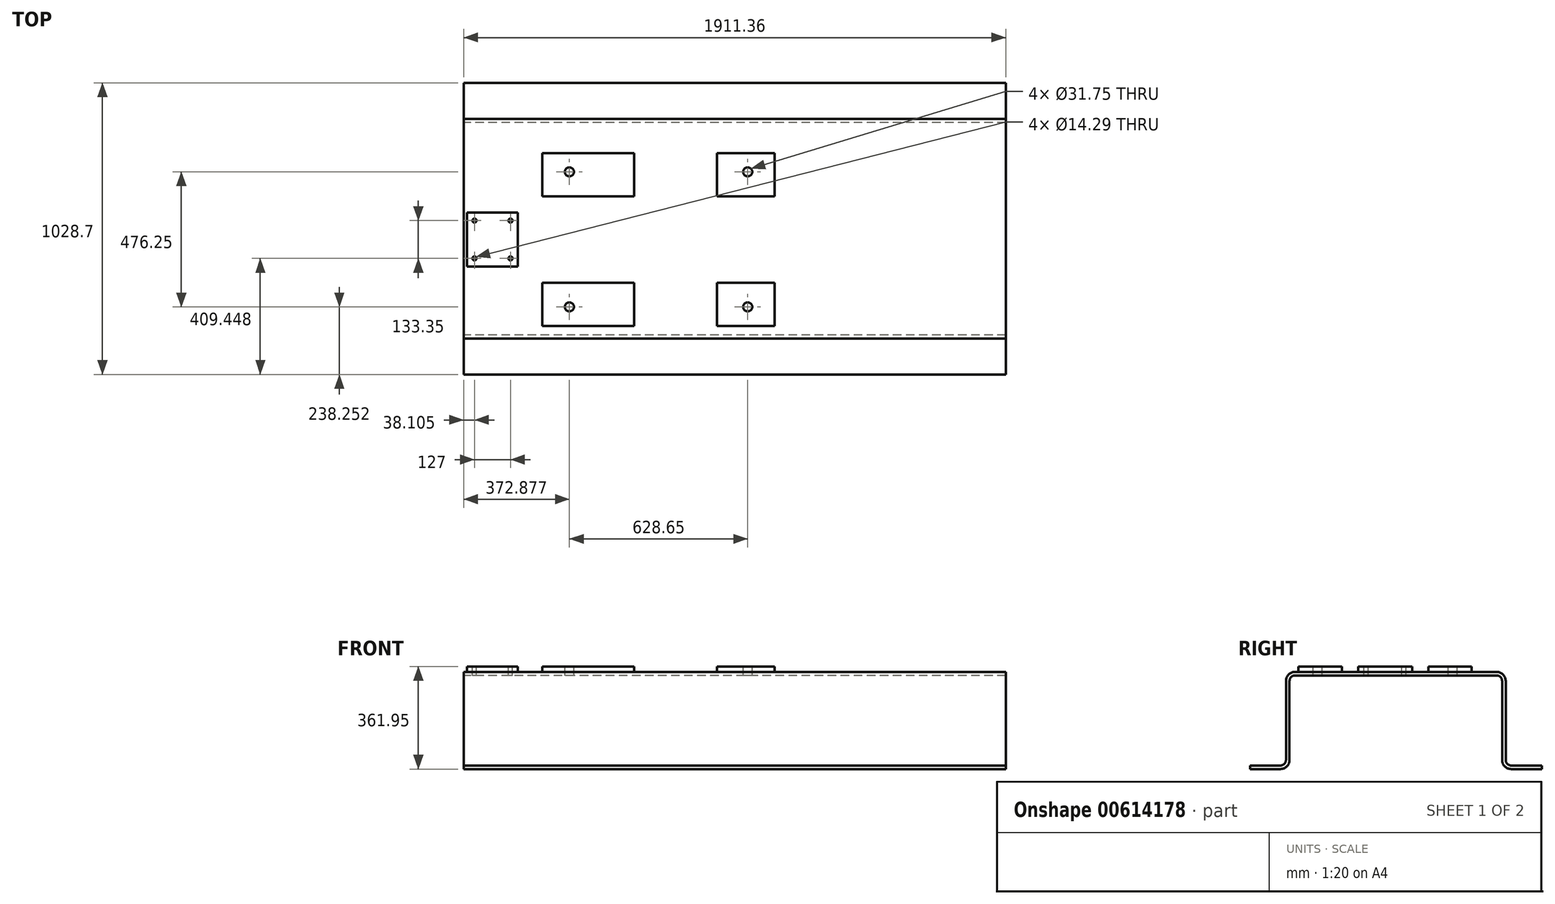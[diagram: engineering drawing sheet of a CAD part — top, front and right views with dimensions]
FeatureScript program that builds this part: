
annotation { "Feature Type Name" : "Feature", "Feature Type Description" : "" }
export const myFeature = defineFeature(function(context is Context, id is Id, definition is map)
    precondition{}
    {
        {
            var Q0;
            Q0=qCreatedBy(makeId("Right.planeOp"),FACE);
            var sketch = newSketch(context, id + "F0", { "sketchPlane" : qUnion([Q0])});
            skLineSegment(sketch, "E0.bottom", {"start": v(-355.6, 171.45) * mm, "end": v(0, 171.45) * mm});
            skLineSegment(sketch, "E0.top", {"start": v(-514.35, -171.45) * mm, "end": v(-406.4, -171.45) * mm});
            skLineSegment(sketch, "E0.left", {"start": v(-514.35, -158.75) * mm, "end": v(-514.35, -171.45) * mm});
            skLineSegment(sketch, "E0.right", {"start": v(514.35, 171.45) * mm, "end": v(514.35, -171.45) * mm});
            skPoint(sketch, "E0.middle", {"position": v(0, 0) * mm});
            skLineSegment(sketch, "E1.0", {"start": v(-387.35, 139.7) * mm, "end": v(-387.35, -139.7) * mm});
            skLineSegment(sketch, "E2", {"start": v(0, 292.84) * mm, "end": v(0, -241.27) * mm, "construction": true});
            skLineSegment(sketch, "E3.0", {"start": v(-355.6, 158.75) * mm, "end": v(0, 158.75) * mm});
            skLineSegment(sketch, "E4.0", {"start": v(-374.65, 139.7) * mm, "end": v(-374.65, -139.7) * mm});
            skLineSegment(sketch, "E5.0", {"start": v(-514.35, -158.75) * mm, "end": v(-406.4, -158.75) * mm});
            skArc(sketch, "E6.filletArc", {"start": v(-406.4, -158.75) * mm, "mid": v(-392.93, -153.17) * mm, "end": v(-387.35, -139.7) * mm});
            skArc(sketch, "E7.filletArc", {"start": v(-355.6, 158.75) * mm, "mid": v(-369.07, 153.17) * mm, "end": v(-374.65, 139.7) * mm});
            skPoint(sketch, "E8.newPointA", {"position": v(514.35, -171.45) * mm});
            skArc(sketch, "E8.filletArc", {"start": v(-406.4, -171.45) * mm, "mid": v(-383.95, -162.15) * mm, "end": v(-374.65, -139.7) * mm});
            skPoint(sketch, "E9.newPointB", {"position": v(-514.35, 171.45) * mm});
            skArc(sketch, "E9.filletArc", {"start": v(-355.6, 171.45) * mm, "mid": v(-378.05, 162.15) * mm, "end": v(-387.35, 139.7) * mm});
            skLineSegment(sketch, "E10", {"start": v(0, 171.45) * mm, "end": v(0, 158.75) * mm});
            skSolve(sketch);
        }
        {
            var Q0;
            Q0 = qSketchRegion(id + "F0", true);
            extrude(context, id + "F1", {"entities" : qUnion([Q0]), "endBound" : BoundingType.SYMMETRIC, "depth" : 1911.35 * mm, "offsetDistance" : 25.4 * mm});
        }
        {
            var Q0;
            Q0=makeQuery(id+"F1.opExtrude","SWEPT_BODY",BODY,{"disambiguationData":[OSD([sQuery(id+"F0.wireOp",EDGE,"E0.bottom"),sQuery(id+"F0.wireOp",EDGE,"E0.top"),sQuery(id+"F0.wireOp",EDGE,"E0.left"),sQuery(id+"F0.wireOp",EDGE,"E1.0"),sQuery(id+"F0.wireOp",EDGE,"E3.0"),sQuery(id+"F0.wireOp",EDGE,"E4.0"),sQuery(id+"F0.wireOp",EDGE,"E5.0"),sQuery(id+"F0.wireOp",EDGE,"E6.filletArc"),sQuery(id+"F0.wireOp",EDGE,"E7.filletArc"),sQuery(id+"F0.wireOp",EDGE,"E8.filletArc"),sQuery(id+"F0.wireOp",EDGE,"E9.filletArc"),sQuery(id+"F0.wireOp",EDGE,"E10")])]});
            var Q1;
            Q1=qCreatedBy(makeId("Front.planeOp"),FACE);
            mirror(context, id + "F2", {"operationType" : NewBodyOperationType.ADD, "entities" : qUnion([Q0]), "mirrorPlane" : qUnion([Q1])});
        }
        {
            var Q0;
            {var subQ0=makeQuery(id+"F1.opExtrude","SWEPT_FACE",FACE,{"disambiguationData":[OSD([sQuery(id+"F0.wireOp",EDGE,"E0.bottom")])]});Q0=makeQuery(id+"F2.boolean.opBoolean","MERGE",FACE,{"derivedFrom":[subQ0,makeQuery(id+"F2.opPattern","COPY",FACE,{"derivedFrom":subQ0,"instanceName":"1"})]});}
            var sketch = newSketch(context, id + "F3", { "sketchPlane" : qUnion([Q0])});
            skLineSegment(sketch, "E11.0", {"start": v(955.68, 165.1) * mm, "end": v(417.16, 165.1) * mm, "construction": true});
            skLineSegment(sketch, "E12.0", {"start": v(293.14, -38.1) * mm, "end": v(-955.68, -38.1) * mm, "construction": true});
            skLineSegment(sketch, "E13.0", {"start": v(141.1, -190.5) * mm, "end": v(-62.1, -190.5) * mm});
            skLineSegment(sketch, "E14.0", {"start": v(141.1, -342.9) * mm, "end": v(-62.1, -342.9) * mm});
            skLineSegment(sketch, "E15.0", {"start": v(141.1, 114.3) * mm, "end": v(-62.1, 114.3) * mm});
            skLineSegment(sketch, "E16.0", {"start": v(141.1, 266.7) * mm, "end": v(-62.1, 266.7) * mm});
            skLineSegment(sketch, "E17.0", {"start": v(644.52, -779.36) * mm, "end": v(644.52, 355.6) * mm, "construction": true});
            skLineSegment(sketch, "E18.0", {"start": v(-268.35, -779.36) * mm, "end": v(-268.35, 355.6) * mm, "construction": true});
            skLineSegment(sketch, "E19.0", {"start": v(-62.1, -342.9) * mm, "end": v(-62.1, -190.5) * mm});
            skLineSegment(sketch, "E20.0", {"start": v(141.1, -342.9) * mm, "end": v(141.1, -190.5) * mm});
            skLineSegment(sketch, "E21.0", {"start": v(-354.2, -342.9) * mm, "end": v(-354.2, -190.5) * mm});
            skLineSegment(sketch, "E22.0", {"start": v(-678.05, -342.9) * mm, "end": v(-678.05, -190.5) * mm});
            skLineSegment(sketch, "E23.trimOffspring", {"start": v(-354.2, 266.7) * mm, "end": v(-678.05, 266.7) * mm});
            skLineSegment(sketch, "E24.trimOffspring", {"start": v(-354.2, 114.3) * mm, "end": v(-678.05, 114.3) * mm});
            skLineSegment(sketch, "E25.trimOffspring", {"start": v(-354.2, -190.5) * mm, "end": v(-678.05, -190.5) * mm});
            skLineSegment(sketch, "E26.trimOffspring", {"start": v(-354.2, -342.9) * mm, "end": v(-678.05, -342.9) * mm});
            skLineSegment(sketch, "E27.trimOffspring", {"start": v(141.1, 114.3) * mm, "end": v(141.1, 266.7) * mm});
            skLineSegment(sketch, "E28.trimOffspring", {"start": v(-62.1, 114.3) * mm, "end": v(-62.1, 266.7) * mm});
            skLineSegment(sketch, "E29.trimOffspring", {"start": v(-678.05, 114.3) * mm, "end": v(-678.05, 266.7) * mm});
            skLineSegment(sketch, "E30.trimOffspring", {"start": v(-354.2, 114.3) * mm, "end": v(-354.2, 266.7) * mm});
            skSolve(sketch);
        }
        {
            var Q0;
            Q0 = qSketchRegion(id + "F3", true);
            extrude(context, id + "F4", {"entities" : qUnion([Q0]), "operationType" : NewBodyOperationType.ADD, "depth" : 19.05 * mm, "offsetDistance" : 25.4 * mm});
        }
        {
            var Q0;
            Q0=makeQuery(id+"F4.opExtrude","CAP_FACE",FACE,{"disambiguationData":[OSD([sQuery(id+"F3.wireOp",EDGE,"E23.trimOffspring"),sQuery(id+"F3.wireOp",EDGE,"E24.trimOffspring"),sQuery(id+"F3.wireOp",EDGE,"E29.trimOffspring"),sQuery(id+"F3.wireOp",EDGE,"E30.trimOffspring")])],"isStart":false});
            var sketch = newSketch(context, id + "F5", { "sketchPlane" : qUnion([Q0])});
            skLineSegment(sketch, "E31.0", {"start": v(-268.35, -779.36) * mm, "end": v(-268.35, 355.6) * mm, "construction": true});
            skLineSegment(sketch, "E32.0", {"start": v(293.14, -38.1) * mm, "end": v(-955.68, -38.1) * mm, "construction": true});
            skLineSegment(sketch, "E33.0", {"start": v(293.14, 200.15) * mm, "end": v(-955.68, 200.15) * mm, "construction": true});
            skLineSegment(sketch, "E34.0", {"start": v(293.14, -276.1) * mm, "end": v(-955.68, -276.1) * mm, "construction": true});
            skLineSegment(sketch, "E35.0", {"start": v(-582.8, -779.36) * mm, "end": v(-582.8, 355.6) * mm, "construction": true});
            skLineSegment(sketch, "E36.0", {"start": v(45.85, -779.36) * mm, "end": v(45.85, 355.6) * mm, "construction": true});
            skPoint(sketch, "E37", {"position": v(-582.8, 200.15) * mm});
            skPoint(sketch, "E38", {"position": v(45.85, 200.15) * mm});
            skPoint(sketch, "E39", {"position": v(45.85, -276.1) * mm});
            skPoint(sketch, "E40", {"position": v(-582.8, -276.1) * mm});
            skSolve(sketch);
        }
        {
            var Q0;
            Q0=sQuery(id+"F5.wireOp",VERTEX,"E37");
            var Q1;
            Q1=sQuery(id+"F5.wireOp",VERTEX,"E40");
            var Q2;
            Q2=sQuery(id+"F5.wireOp",VERTEX,"E38");
            var Q3;
            Q3=sQuery(id+"F5.wireOp",VERTEX,"E39");
            var Q4;
            Q4=makeQuery(id+"F1.opExtrude","SWEPT_BODY",BODY,{"disambiguationData":[OSD([sQuery(id+"F0.wireOp",EDGE,"E0.bottom"),sQuery(id+"F0.wireOp",EDGE,"E0.top"),sQuery(id+"F0.wireOp",EDGE,"E0.left"),sQuery(id+"F0.wireOp",EDGE,"E1.0"),sQuery(id+"F0.wireOp",EDGE,"E3.0"),sQuery(id+"F0.wireOp",EDGE,"E4.0"),sQuery(id+"F0.wireOp",EDGE,"E5.0"),sQuery(id+"F0.wireOp",EDGE,"E6.filletArc"),sQuery(id+"F0.wireOp",EDGE,"E7.filletArc"),sQuery(id+"F0.wireOp",EDGE,"E8.filletArc"),sQuery(id+"F0.wireOp",EDGE,"E9.filletArc"),sQuery(id+"F0.wireOp",EDGE,"E10")])]});
            hole(context, id + "F6", {"style" : HoleStyle.SIMPLE, "endStyle" : HoleEndStyle.THROUGH, "holeDiameter" : 31.75 * mm, "majorDiameter" : 9.52 * mm, "isTappedThrough" : true, "tappedDepth" : 25.4 * mm, "tapClearance" : 3, "locations" : qUnion([Q0, Q1, Q2, Q3]), "scope" : qUnion([Q4])});
        }
        {
            var Q0;
            Q0=makeQuery(id+"F3.imprint","IMPRINT",FACE,{"disambiguationData":[TD([[makeQuery(id+"F3.imprint","IMPRINT",EDGE,{"derivedFrom":sQuery(id+"F3.wireOp",EDGE,"E13.0")}),-1.0]])]});
            var sketch = newSketch(context, id + "F7", { "sketchPlane" : qUnion([Q0])});
            skLineSegment(sketch, "E41.0", {"start": v(293.14, -38.1) * mm, "end": v(-955.68, -38.1) * mm, "construction": true});
            skLineSegment(sketch, "E42.0", {"start": v(-678.05, -38.1) * mm, "end": v(-678.05, 266.7) * mm, "construction": true});
            skPoint(sketch, "E43.orphan", {"position": v(-678.05, 114.3) * mm});
            skLineSegment(sketch, "E44.0", {"start": v(-765.43, -38.1) * mm, "end": v(-765.43, 57.15) * mm});
            skLineSegment(sketch, "E45.0", {"start": v(-943.23, -38.1) * mm, "end": v(-943.23, 57.15) * mm});
            skLineSegment(sketch, "E46.0", {"start": v(-765.43, 57.15) * mm, "end": v(-943.23, 57.15) * mm});
            skLineSegment(sketch, "E47.MirrorCS", {"start": v(-765.43, -38.1) * mm, "end": v(-765.43, -133.35) * mm});
            skLineSegment(sketch, "E48.MirrorCS", {"start": v(-765.43, -133.35) * mm, "end": v(-943.23, -133.35) * mm});
            skLineSegment(sketch, "E49.MirrorCS", {"start": v(-943.23, -38.1) * mm, "end": v(-943.23, -133.35) * mm});
            skSolve(sketch);
        }
        {
            var Q0;
            Q0 = qSketchRegion(id + "F7", true);
            extrude(context, id + "F8", {"entities" : qUnion([Q0]), "operationType" : NewBodyOperationType.ADD, "depth" : 19.05 * mm, "offsetDistance" : 25.4 * mm});
        }
        {
            var Q0;
            Q0=makeQuery(id+"F8.opExtrude","CAP_FACE",FACE,{"disambiguationData":[OSD([sQuery(id+"F7.wireOp",EDGE,"E44.0"),sQuery(id+"F7.wireOp",EDGE,"E45.0"),sQuery(id+"F7.wireOp",EDGE,"E46.0"),sQuery(id+"F7.wireOp",EDGE,"E47.MirrorCS"),sQuery(id+"F7.wireOp",EDGE,"E48.MirrorCS"),sQuery(id+"F7.wireOp",EDGE,"E49.MirrorCS")])],"isStart":false});
            var sketch = newSketch(context, id + "F9", { "sketchPlane" : qUnion([Q0])});
            skLineSegment(sketch, "E50.0", {"start": v(293.14, -38.1) * mm, "end": v(-955.68, -38.1) * mm, "construction": true});
            skLineSegment(sketch, "E51.0", {"start": v(-268.35, -779.36) * mm, "end": v(-268.35, 355.6) * mm, "construction": true});
            skLineSegment(sketch, "E52.0", {"start": v(-790.58, -779.36) * mm, "end": v(-790.58, 355.6) * mm, "construction": true});
            skLineSegment(sketch, "E53.0", {"start": v(-917.58, -779.36) * mm, "end": v(-917.58, 355.6) * mm, "construction": true});
            skLineSegment(sketch, "E54.0", {"start": v(293.14, 28.45) * mm, "end": v(-955.68, 28.45) * mm, "construction": true});
            skLineSegment(sketch, "E55.0", {"start": v(293.14, -104.9) * mm, "end": v(-955.68, -104.9) * mm, "construction": true});
            skPoint(sketch, "E56", {"position": v(-917.58, 28.45) * mm});
            skPoint(sketch, "E57", {"position": v(-790.58, 28.45) * mm});
            skPoint(sketch, "E58", {"position": v(-790.58, -104.9) * mm});
            skPoint(sketch, "E59", {"position": v(-917.58, -104.9) * mm});
            skSolve(sketch);
        }
        {
            var Q0;
            Q0=sQuery(id+"F9.wireOp",VERTEX,"E56");
            var Q1;
            Q1=sQuery(id+"F9.wireOp",VERTEX,"E57");
            var Q2;
            Q2=sQuery(id+"F9.wireOp",VERTEX,"E59");
            var Q3;
            Q3=sQuery(id+"F9.wireOp",VERTEX,"E58");
            var Q4;
            Q4=makeQuery(id+"F1.opExtrude","SWEPT_BODY",BODY,{"disambiguationData":[OSD([sQuery(id+"F0.wireOp",EDGE,"E0.bottom"),sQuery(id+"F0.wireOp",EDGE,"E0.top"),sQuery(id+"F0.wireOp",EDGE,"E0.left"),sQuery(id+"F0.wireOp",EDGE,"E1.0"),sQuery(id+"F0.wireOp",EDGE,"E3.0"),sQuery(id+"F0.wireOp",EDGE,"E4.0"),sQuery(id+"F0.wireOp",EDGE,"E5.0"),sQuery(id+"F0.wireOp",EDGE,"E6.filletArc"),sQuery(id+"F0.wireOp",EDGE,"E7.filletArc"),sQuery(id+"F0.wireOp",EDGE,"E8.filletArc"),sQuery(id+"F0.wireOp",EDGE,"E9.filletArc"),sQuery(id+"F0.wireOp",EDGE,"E10")])]});
            hole(context, id + "F10", {"style" : HoleStyle.SIMPLE, "endStyle" : HoleEndStyle.THROUGH, "holeDiameter" : 14.29 * mm, "majorDiameter" : 6.35 * mm, "isTappedThrough" : true, "tappedDepth" : 25.4 * mm, "tapClearance" : 3, "locations" : qUnion([Q0, Q1, Q2, Q3]), "scope" : qUnion([Q4])});
        }
    });
